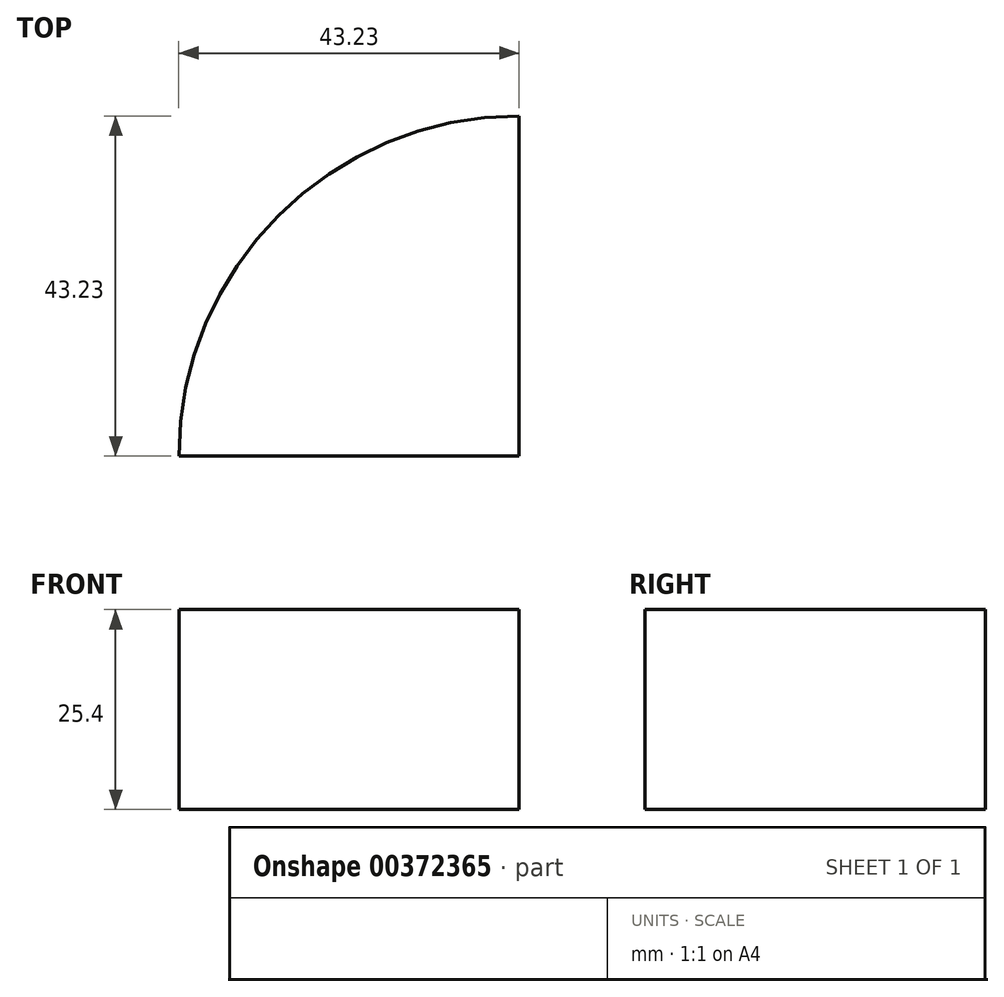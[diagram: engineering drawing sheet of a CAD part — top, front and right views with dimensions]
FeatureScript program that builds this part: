
annotation { "Feature Type Name" : "Feature", "Feature Type Description" : "" }
export const myFeature = defineFeature(function(context is Context, id is Id, definition is map)
    precondition{}
    {
        {
            var Q0;
            Q0=qCreatedBy(makeId("Top.planeOp"),FACE);
            var sketch = newSketch(context, id + "F0", { "sketchPlane" : qUnion([Q0])});
            skCircle(sketch, "E0", {"center": v(0, 0) * mm, "radius": 43.23 * mm});
            skLineSegment(sketch, "E1", {"start": v(-43.23, 0) * mm, "end": v(0, 0) * mm});
            skLineSegment(sketch, "E2", {"start": v(0, 0) * mm, "end": v(0, 43.23) * mm});
            skSolve(sketch);
        }
        {
            var Q0;
            {var subQ0=sQuery(id+"F0.wireOp",EDGE,"E1");Q0=makeQuery(id+"F0.imprint","IMPRINT",FACE,{"disambiguationData":[TD([[makeQuery(id+"F0.imprint","IMPRINT",EDGE,{"derivedFrom":subQ0}),1.0]])]});}
            extrude(context, id + "F1", {"entities" : qUnion([Q0]), "depth" : 25.4 * mm});
        }
    });
